# Revit family: Bjælke - KB(B)E
name_source: partatom
category: Structural Framing
units: mm (PartAtom-declared; Revit-internal decimal feet)

## family parameters
Always export as geometry = No
Always vertical = Yes
Cut with Voids When Loaded = No
Material for Model Behavior = Other
OmniClass Number = 23.25.30.11.14.14
OmniClass Title = Beams
Section Shape = Not Defined
Shared = No
Show family pre-cut in plan views = Yes

## types (2) — shared parameters
Bred Hylde = No
CRH_RFA_TimeStamp_LastRelease = 20191107
Hylde Bredde = 150 mm
Hylde Højde 1 = 180 mm  [stored 0.590551 ft]
Højde = 380 mm
Kommentar = Bred hylde kan kun udføres på bredt element
Manufacturer = CRH Concrete

## per-type parameters (varying)
| type | Bredde | Bredde 2 | Bredt Element | Model |
| KBE 38/18 | 360 mm  [stored 1.1811 ft] | 110 mm  [stored 0.360892 ft] | No | KBE |
| KBBE 38/18 | 500 mm  [stored 1.64042 ft] | 170 mm  [stored 0.557743 ft] | Yes | KBBE |

note: [stored X ft] marks values corroborated as IEEE doubles in the binary element streams (Revit-internal decimal feet)

## geometry (parser evidence)
native form markers: Sweep x4
no freeform markers — native parametric forms only
